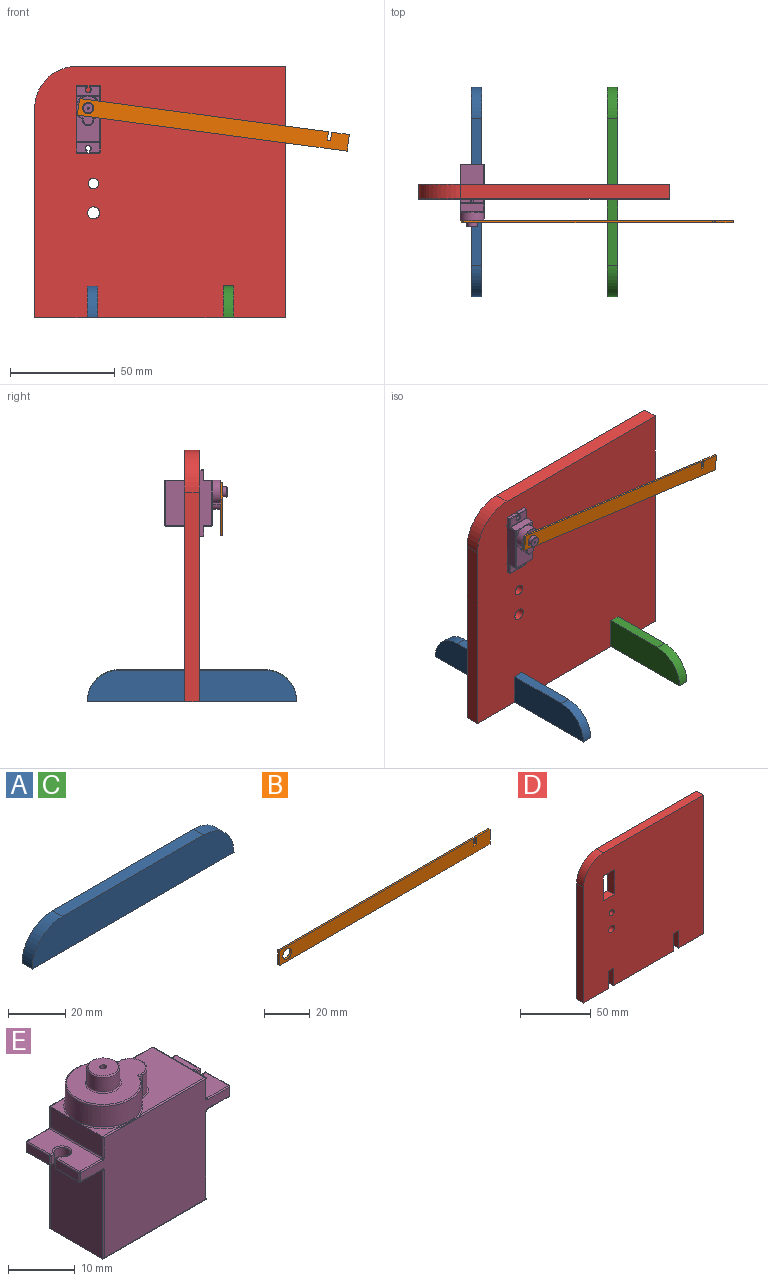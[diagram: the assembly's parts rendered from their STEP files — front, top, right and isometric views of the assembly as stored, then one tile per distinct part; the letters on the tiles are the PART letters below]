
ASSEMBLY  parts=5 mates=3
PART A: 6 faces, bbox 100x5x15 mm
  f0: cylinder r=15mm len=15mm, axis (0,1,0), area 117.8mm2, adj f1,f3,f4,f5
  f1: plane 70x5mm, normal (0,0,1), area 350mm2, adj f0,f2,f4,f5
  f2: cylinder r=15mm len=15mm, axis (0,1,0), area 117.8mm2, adj f1,f3,f4,f5
  f3: plane 100x5mm, normal (0,0,-1), area 500mm2, adj f0,f2,f4,f5
  f4: plane 100x15mm, normal (0,-1,0), area 1403.4mm2, adj f0,f1,f2,f3
  f5: plane 100x15mm, normal (0,1,0), area 1403.4mm2, adj f0,f1,f2,f3
PART B: 11 faces, bbox 130x1x8 mm
  f0: plane 4x1mm, normal (1,0,0), area 4mm2, adj f1,f8,f9,f10
  f1: plane 120x1mm, normal (0,0,1), area 120mm2, adj f0,f2,f9,f10
  f2: plane 8x1mm, normal (-1,0,0), area 8mm2, adj f1,f3,f9,f10
  f3: plane 130x1mm, normal (0,0,-1), area 130mm2, adj f2,f4,f9,f10
  f4: plane 8x1mm, normal (1,0,0), area 8mm2, adj f3,f5,f9,f10
  f5: plane 8.5x1mm, normal (0,0,1), area 8.5mm2, adj f4,f6,f9,f10
  f6: plane 4x1mm, normal (-1,0,0), area 4mm2, adj f5,f8,f9,f10
  f7: cylinder r=2.7mm len=5.4mm, axis (0,1,0), area 17mm2, adj f9,f10
  f8: plane 1.5x1mm, normal (0,0,1), area 1.5mm2, adj f0,f6,f9,f10
  f9: plane 130x8mm, normal (0,-1,0), area 1011.1mm2, adj f0,f1,f2,f3,f4,f5,f6,f7
  f10: plane 130x8mm, normal (0,1,0), area 1011.1mm2, adj f0,f1,f2,f3,f4,f5,f6,f7
PART C: same geometry as A
PART D: 21 faces, bbox 120x7x120 mm
  f0: plane 25.01x7mm, normal (0,0,-1), area 175.1mm2, adj f1,f18,f19,f20
  f1: plane 15x7mm, normal (1,0,0), area 105mm2, adj f0,f2,f19,f20
  f2: plane 7x5mm, normal (0,0,-1), area 35mm2, adj f1,f3,f19,f20
  f3: plane 15x7mm, normal (-1,0,0), area 105mm2, adj f2,f4,f19,f20
  f4: plane 59.97x7mm, normal (0,0,-1), area 419.8mm2, adj f3,f5,f19,f20
  f5: plane 15x7mm, normal (1,0,0), area 105mm2, adj f4,f6,f19,f20
  f6: plane 7x5mm, normal (0,0,-1), area 35mm2, adj f5,f7,f19,f20
  f7: plane 15x7mm, normal (-1,0,0), area 105mm2, adj f6,f8,f19,f20
  f8: plane 25.01x7mm, normal (0,0,-1), area 175.1mm2, adj f7,f9,f19,f20
  f9: plane 120x7mm, normal (1,0,0), area 840mm2, adj f8,f10,f19,f20
  f10: plane 100x7mm, normal (0,0,1), area 700mm2, adj f9,f11,f19,f20
  f11: cylinder r=20mm len=20mm, axis (0,1,0), area 219.9mm2, adj f10,f18,f19,f20
  f12: plane 11x7mm, normal (0,0,-1), area 77mm2, adj f13,f15,f19,f20
  f13: plane 21.6x7mm, normal (-1,0,0), area 151.2mm2, adj f12,f14,f19,f20
  f14: plane 11x7mm, normal (0,0,1), area 77mm2, adj f13,f15,f19,f20
  f15: plane 21.6x7mm, normal (1,0,0), area 151.2mm2, adj f12,f14,f19,f20
  f16: cylinder r=2.5mm len=7mm, axis (0,1,0), area 110mm2, adj f19,f20
  f17: cylinder r=2.88mm len=7mm, axis (0,1,0), area 126.9mm2, adj f19,f20
  f18: plane 100x7mm, normal (-1,0,0), area 700mm2, adj f0,f11,f19,f20
  f19: plane 120x120mm, normal (0,-1,0), area 13880.8mm2, adj f0,f1,f2,f3,f4,f5,f6,f7
  f20: plane 120x120mm, normal (0,1,0), area 13880.8mm2, adj f0,f1,f2,f3,f4,f5,f6,f7
PART E: 138 faces, bbox 32.1x12.6x29.8 mm
  f0: plane 13.6x11.1mm, normal (0,0,1), area 83.8mm2, adj f133,f134,f135,f136,f137
  f1: plane 4.02x3.61mm, normal (0,0,1), area 4.9mm2, adj f9,f99,f100
  f2: plane 13.91x11.1mm, normal (0,0,1), area 112.2mm2, adj f113,f114,f119,f122,f123,f126,f128,f129
  f3: plane 4.85x1.6mm, normal (-1,0,0), area 7.8mm2, adj f63,f64,f83,f84
  f4: plane 5.05x1.6mm, normal (1,0,0), area 8.1mm2, adj f20,f79,f95,f96
  f5: plane 16.1x11.1mm, normal (1,0,0), area 178.7mm2, adj f46,f47,f57,f58
  f6: plane 16.3x11.1mm, normal (-1,0,0), area 180.9mm2, adj f12,f48,f67,f68
  f7: plane 11.1x3.6mm, normal (1,0,0), area 40mm2, adj f111,f112,f121,f122
  f8: plane 31.6x22.1mm, normal (0,1,0), area 493.5mm2, adj f36,f37,f56,f57,f68,f69,f77,f78
  f9: plane 11.24x3.94mm, normal (-1,0,0), area 42.2mm2, adj f1,f11,f98,f101,f115,f124,f131
  f10: plane 31.6x22.1mm, normal (0,-1,0), area 493.5mm2, adj f41,f42,f45,f47,f48,f54,f55,f61
  f11: plane 4.02x3.61mm, normal (0,0,1), area 4.9mm2, adj f9,f127,f132
  f12: plane 21.8x11.1mm, normal (0,0,-1), area 242mm2, adj f6,f45,f46,f56
  f13: plane 4.85x1.6mm, normal (-1,0,0), area 7.8mm2, adj f86,f87,f103,f104
  f14: plane 11.1x4.6mm, normal (0,0,-1), area 43.9mm2, adj f51,f53,f62,f63,f66,f67,f87,f88
  f15: plane 11.1x4.6mm, normal (0,0,1), area 43.9mm2, adj f65,f75,f84,f85,f102,f103,f115,f116
  f16: plane 11.1x4.6mm, normal (0,0,-1), area 43.9mm2, adj f49,f58,f59,f60,f61,f70,f78,f79
  f17: plane 11.1x4.6mm, normal (0,0,1), area 43.9mm2, adj f71,f80,f81,f90,f96,f97,f110,f111
  f18: plane 5.05x1.6mm, normal (1,0,0), area 8.1mm2, adj f21,f60,f81,f82
  f19: cylinder r=1.25mm len=2.5mm, axis (0,0,1), area 10.9mm2, adj f20,f21,f59,f80
  f20: plane 1.6x0.85mm, normal (0,-1,0), area 1.4mm2, adj f4,f19,f70,f90
  f21: plane 1.6x0.85mm, normal (0,1,0), area 1.4mm2, adj f18,f19,f49,f71
  f22: cylinder r=1.25mm len=2.5mm, axis (0,0,1), area 10.9mm2, adj f23,f24,f53,f75
  f23: plane 1.6x0.65mm, normal (0,1,0), area 1mm2, adj f22,f51,f64,f65
  f24: plane 1.6x0.65mm, normal (0,-1,0), area 1mm2, adj f22,f66,f85,f86
  f25: cylinder r=2.5mm len=5mm, axis (0,0,-1), area 29.8mm2, adj f26,f28,f123,f136
  f26: plane 3.8x0.57mm, normal (0,1,0), area 2.2mm2, adj f25,f27,f126,f134
  f27: cylinder r=5.75mm len=11.5mm, axis (0,0,-1), area 117.9mm2, adj f26,f28,f34,f39,f98,f100,f107,f114
  f28: plane 3.8x0.57mm, normal (0,-1,0), area 2.2mm2, adj f25,f27,f119,f137
  f29: cylinder r=2.5mm len=5mm, axis (0,0,-1), area 40.8mm2, adj f31,f133
  f30: plane 4.6x4.6mm, normal (0,0,1), area 15.8mm2, adj f31,f32
  f31: cone r=2.3mm half-angle=45deg, axis (0,0,-1), area 4.3mm2, adj f29,f30
  f32: cylinder r=0.5mm len=3mm, axis (0,0,1), area 9.4mm2, adj f30,f33
  f33: plane 1x1mm, normal (0,0,1), area 0.8mm2, adj f32
  f34: bspline ~2.08x0.39mm, area 0.3mm2, adj f27,f35,f129,f130
  f35: bspline ~2.14x0.33mm, area 0.3mm2, adj f34,f36,f128,f129
  f36: bspline ~2.14x0.2mm, area 0.4mm2, adj f8,f35,f37,f128
  f37: bspline ~2.14x0.2mm, area 0.4mm2, adj f8,f36,f38,f127
  f38: bspline ~2.14x0.33mm, area 0.3mm2, adj f37,f127,f130,f132
  f39: bspline ~2.08x0.39mm, area 0.3mm2, adj f27,f40,f100,f107
  f40: bspline ~2.14x0.33mm, area 0.3mm2, adj f39,f41,f99,f100
  f41: bspline ~2.14x0.2mm, area 0.4mm2, adj f10,f40,f42,f99
  f42: bspline ~2.14x0.2mm, area 0.4mm2, adj f10,f41,f43,f113
  f43: bspline ~2.14x0.33mm, area 0.3mm2, adj f42,f107,f113,f114
  f44: sphere r=0.2mm, area 0.1mm2, adj f45,f46,f47
  f45: cylinder r=0.2mm len=21.8mm, axis (1,0,0), area 6.8mm2, adj f10,f12,f44,f48
  f46: cylinder r=0.2mm len=11.1mm, axis (0,1,0), area 3.5mm2, adj f5,f12,f44,f50
  f47: cylinder r=0.2mm len=16.1mm, axis (0,0,-1), area 5.1mm2, adj f5,f10,f44,f54
  f48: cylinder r=0.2mm len=16.3mm, axis (0,0,-1), area 5.1mm2, adj f6,f10,f45,f55
  f49: cylinder r=0.2mm len=0.85mm, axis (1,0,0), area 0.2mm2, adj f16,f21,f59,f60
  f50: sphere r=0.2mm, area 0mm2, adj f46,f56,f57
  f51: cylinder r=0.2mm len=0.65mm, axis (1,0,0), area 0.2mm2, adj f14,f23,f52,f53
  f52: sphere r=0.2mm, area 0.1mm2, adj f51,f63,f64
  f53: torus R=1.45mm, axis (0,0,1), area 2.2mm2, adj f14,f22,f51,f66
  f54: torus R=0.4mm, axis (0,1,0), area 0.1mm2, adj f10,f47,f58,f61
  f55: torus R=0.4mm, axis (0,1,0), area 0.1mm2, adj f10,f48,f62,f67
  f56: cylinder r=0.2mm len=21.8mm, axis (-1,0,0), area 6.8mm2, adj f8,f12,f50,f68
  f57: cylinder r=0.2mm len=16.1mm, axis (0,0,-1), area 5.1mm2, adj f5,f8,f50,f69
  f58: cylinder r=0.2mm len=11.1mm, axis (0,-1,0), area 3.5mm2, adj f5,f16,f54,f69
  f59: torus R=1.45mm, axis (0,0,1), area 2.2mm2, adj f16,f19,f49,f70
  f60: cylinder r=0.2mm len=5.05mm, axis (0,-1,0), area 1.6mm2, adj f16,f18,f49,f72
  f61: cylinder r=0.2mm len=4.6mm, axis (1,0,0), area 1.4mm2, adj f10,f16,f54,f72
  f62: cylinder r=0.2mm len=4.6mm, axis (1,0,0), area 1.4mm2, adj f10,f14,f55,f73
  f63: cylinder r=0.2mm len=4.85mm, axis (0,1,0), area 1.5mm2, adj f3,f14,f52,f73
  f64: cylinder r=0.2mm len=1.6mm, axis (0,0,-1), area 0.5mm2, adj f3,f23,f52,f74
  f65: cylinder r=0.2mm len=0.65mm, axis (-1,0,0), area 0.2mm2, adj f15,f23,f74,f75
  f66: cylinder r=0.2mm len=0.65mm, axis (-1,0,0), area 0.2mm2, adj f14,f24,f53,f76
  f67: cylinder r=0.2mm len=11.1mm, axis (0,1,0), area 3.5mm2, adj f6,f14,f55,f77
  f68: cylinder r=0.2mm len=16.3mm, axis (0,0,-1), area 5.1mm2, adj f6,f8,f56,f77
  f69: torus R=0.4mm, axis (0,-1,0), area 0.1mm2, adj f8,f57,f58,f78
  f70: cylinder r=0.2mm len=0.85mm, axis (-1,0,0), area 0.2mm2, adj f16,f20,f59,f79
  f71: cylinder r=0.2mm len=0.85mm, axis (-1,0,0), area 0.2mm2, adj f17,f21,f80,f81
  f72: sphere r=0.2mm, area 0.1mm2, adj f60,f61,f82
  f73: sphere r=0.2mm, area 0mm2, adj f62,f63,f83
  f74: sphere r=0.2mm, area 0.1mm2, adj f64,f65,f84
  f75: torus R=1.45mm, axis (0,0,1), area 2.2mm2, adj f15,f22,f65,f85
  f76: sphere r=0.2mm, area 0.1mm2, adj f66,f86,f87
  f77: torus R=0.4mm, axis (0,-1,0), area 0.1mm2, adj f8,f67,f68,f88
  f78: cylinder r=0.2mm len=4.6mm, axis (-1,0,0), area 1.4mm2, adj f8,f16,f69,f89
  f79: cylinder r=0.2mm len=5.05mm, axis (0,-1,0), area 1.6mm2, adj f4,f16,f70,f89
  f80: torus R=1.45mm, axis (0,0,1), area 2.2mm2, adj f17,f19,f71,f90
  f81: cylinder r=0.2mm len=5.05mm, axis (0,1,0), area 1.6mm2, adj f17,f18,f71,f91
  f82: cylinder r=0.2mm len=1.6mm, axis (0,0,-1), area 0.5mm2, adj f10,f18,f72,f91
  f83: cylinder r=0.2mm len=1.6mm, axis (0,0,-1), area 0.5mm2, adj f3,f10,f73,f92
  f84: cylinder r=0.2mm len=4.85mm, axis (0,-1,0), area 1.5mm2, adj f3,f15,f74,f92
  f85: cylinder r=0.2mm len=0.65mm, axis (1,0,0), area 0.2mm2, adj f15,f24,f75,f93
  f86: cylinder r=0.2mm len=1.6mm, axis (0,0,-1), area 0.5mm2, adj f13,f24,f76,f93
  f87: cylinder r=0.2mm len=4.85mm, axis (0,1,0), area 1.5mm2, adj f13,f14,f76,f94
  f88: cylinder r=0.2mm len=4.6mm, axis (-1,0,0), area 1.4mm2, adj f8,f14,f77,f94
  f89: sphere r=0.2mm, area 0mm2, adj f78,f79,f95
  f90: cylinder r=0.2mm len=0.85mm, axis (1,0,0), area 0.2mm2, adj f17,f20,f80,f96
  f91: sphere r=0.2mm, area 0.1mm2, adj f81,f82,f97
  f92: sphere r=0.2mm, area 0.1mm2, adj f83,f84,f102
  f93: sphere r=0.2mm, area 0.1mm2, adj f85,f86,f103
  f94: sphere r=0.2mm, area 0.1mm2, adj f87,f88,f104
  f95: cylinder r=0.2mm len=1.6mm, axis (0,0,-1), area 0.5mm2, adj f4,f8,f89,f105
  f96: cylinder r=0.2mm len=5.05mm, axis (0,1,0), area 1.6mm2, adj f4,f17,f90,f105
  f97: cylinder r=0.2mm len=4.6mm, axis (-1,0,0), area 1.4mm2, adj f10,f17,f91,f106
  f98: bspline ~1.57x0.21mm, area 0.2mm2, adj f9,f27,f100
  f99: cylinder r=0.2mm len=3.62mm, axis (-1,0,0), area 1.1mm2, adj f1,f10,f40,f41,f101
  f100: torus R=5.95mm, axis (0,0,1), area 1.7mm2, adj f1,f27,f39,f40,f98
  f101: cylinder r=0.2mm len=3.8mm, axis (0,0,-1), area 1.2mm2, adj f9,f10,f99,f108
  f102: cylinder r=0.2mm len=4.6mm, axis (-1,0,0), area 1.4mm2, adj f10,f15,f92,f108
  f103: cylinder r=0.2mm len=4.85mm, axis (0,-1,0), area 1.5mm2, adj f13,f15,f93,f109
  f104: cylinder r=0.2mm len=1.6mm, axis (0,0,-1), area 0.5mm2, adj f8,f13,f94,f109
  f105: sphere r=0.2mm, area 0mm2, adj f95,f96,f110
  f106: torus R=0.4mm, axis (0,1,0), area 0.1mm2, adj f10,f97,f111,f112
  f107: bspline ~2.08x0.39mm, area 0.3mm2, adj f27,f39,f43,f114
  f108: torus R=0.4mm, axis (0,1,0), area 0.1mm2, adj f10,f101,f102,f115
  f109: sphere r=0.2mm, area 0.1mm2, adj f103,f104,f116
  f110: cylinder r=0.2mm len=4.6mm, axis (1,0,0), area 1.4mm2, adj f8,f17,f105,f117
  f111: cylinder r=0.2mm len=11.1mm, axis (0,1,0), area 3.5mm2, adj f7,f17,f106,f117
  f112: cylinder r=0.2mm len=3.6mm, axis (0,0,-1), area 1.1mm2, adj f7,f10,f106,f118
  f113: cylinder r=0.2mm len=13.92mm, axis (-1,0,0), area 4.4mm2, adj f2,f10,f42,f43,f118
  f114: torus R=5.95mm, axis (0,0,1), area 1.4mm2, adj f2,f27,f43,f107,f119
  f115: cylinder r=0.2mm len=11.1mm, axis (0,-1,0), area 3.5mm2, adj f9,f15,f108,f120
  f116: cylinder r=0.2mm len=4.6mm, axis (1,0,0), area 1.4mm2, adj f8,f15,f109,f120
  f117: torus R=0.4mm, axis (0,-1,0), area 0.1mm2, adj f8,f110,f111,f121
  f118: sphere r=0.2mm, area 0.1mm2, adj f112,f113,f122
  f119: cylinder r=0.2mm len=0.57mm, axis (1,0,0), area 0.2mm2, adj f2,f28,f114,f123
  f120: torus R=0.4mm, axis (0,-1,0), area 0.1mm2, adj f8,f115,f116,f124
  f121: cylinder r=0.2mm len=3.6mm, axis (0,0,-1), area 1.1mm2, adj f7,f8,f117,f125
  f122: cylinder r=0.2mm len=11.1mm, axis (0,-1,0), area 3.5mm2, adj f2,f7,f118,f125
  f123: torus R=2.7mm, axis (0,0,1), area 2.5mm2, adj f2,f25,f119,f126
  f124: cylinder r=0.2mm len=3.8mm, axis (0,0,-1), area 1.2mm2, adj f8,f9,f120,f127
  f125: sphere r=0.2mm, area 0mm2, adj f121,f122,f128
  f126: cylinder r=0.2mm len=0.57mm, axis (-1,0,0), area 0.2mm2, adj f2,f26,f123,f129
  f127: cylinder r=0.2mm len=3.62mm, axis (1,0,0), area 1.1mm2, adj f8,f11,f37,f38,f124
  f128: cylinder r=0.2mm len=13.92mm, axis (1,0,0), area 4.4mm2, adj f2,f8,f35,f36,f125
  f129: torus R=5.95mm, axis (0,0,1), area 1.4mm2, adj f2,f27,f34,f35,f126
  f130: bspline ~2.08x0.39mm, area 0.3mm2, adj f27,f34,f38,f132
  f131: bspline ~1.57x0.21mm, area 0.2mm2, adj f9,f27,f132
  f132: torus R=5.95mm, axis (0,0,1), area 1.7mm2, adj f11,f27,f38,f130,f131
  f133: torus R=2.7mm, axis (0,0,-1), area 5.1mm2, adj f0,f29
  f134: cylinder r=0.2mm len=0.7mm, axis (-1,0,0), area 0.2mm2, adj f0,f26,f135,f136
  f135: torus R=5.55mm, axis (0,0,-1), area 9.6mm2, adj f0,f27,f134,f137
  f136: torus R=2.3mm, axis (0,0,-1), area 2.4mm2, adj f0,f25,f134,f137
  f137: cylinder r=0.2mm len=0.7mm, axis (1,0,0), area 0.2mm2, adj f0,f28,f135,f136
PLACE A rot(axis=(0,0,-1),90deg) t=(-60.23,-46.67,-72.6)mm
PLACE B rot(axis=(0,1,0),7.6deg) t=(-105.78,-19,76.18)mm
PLACE C rot(axis=(0,0,-1),90deg) t=(4.74,-46.67,-72.32)mm
PLACE D t=(0,-1.7,0)mm fixed
PLACE E rot(axis=(0.58,0.58,-0.58),120deg) t=(-70.46,7.7,30.52)mm fixed
MATE revolute B.f7 <-> E.f27  axis (0,-1,0) through (-64.71,-20,46.77)mm
MATE fastened C.f5 <-> D.f7  axis (1,0,0) through (4.74,-5.2,-45.81)mm
MATE fastened A.f5 <-> D.f3  axis (1,0,0) through (-60.23,-5.2,-38.31)mm
